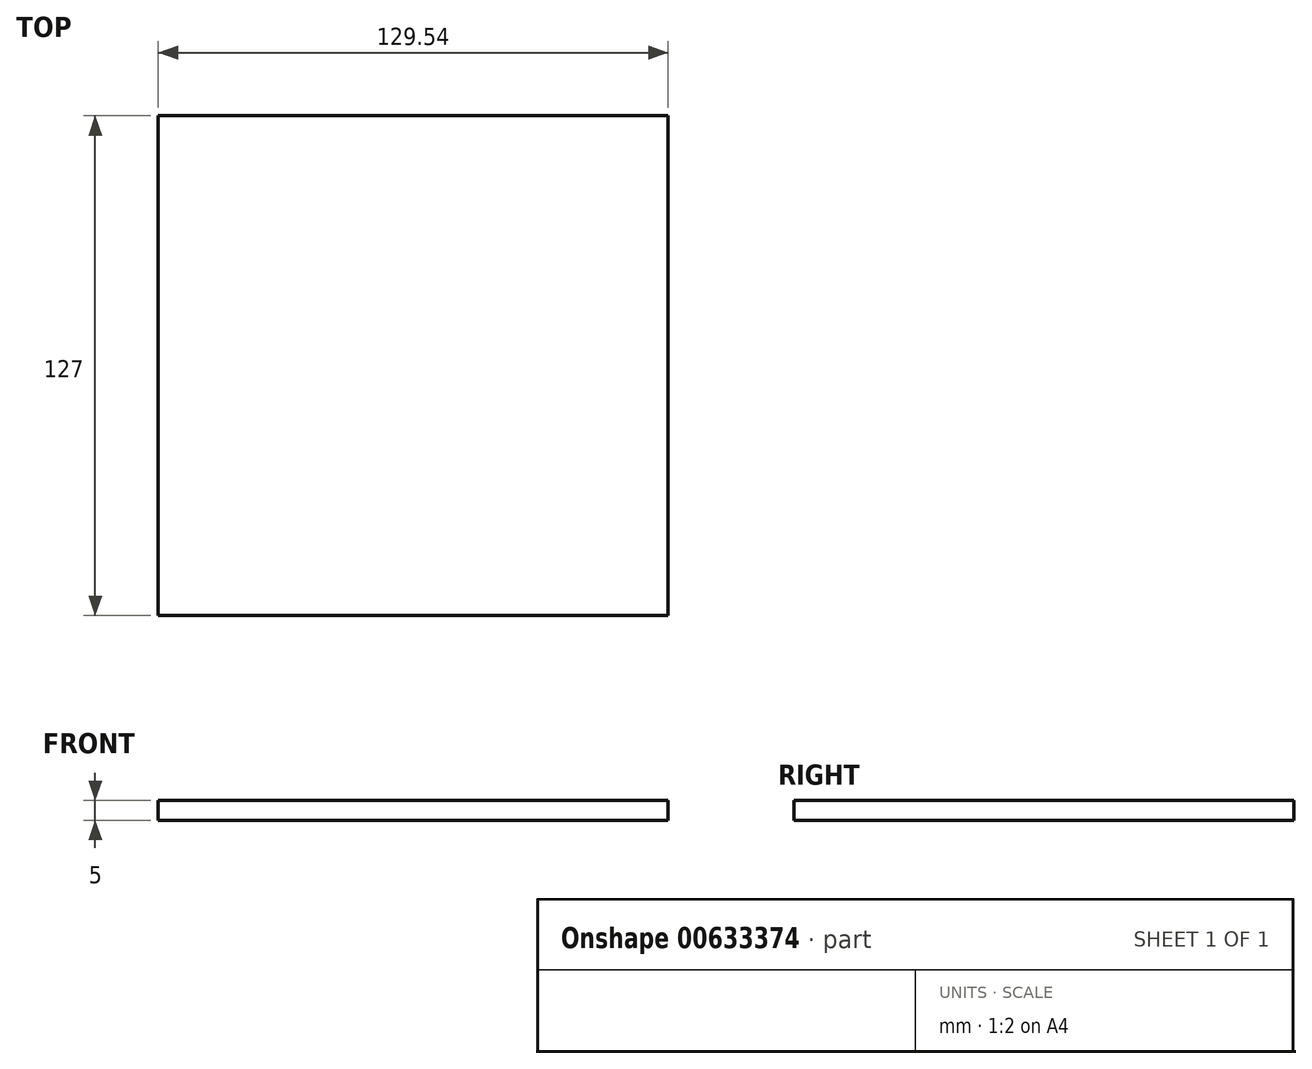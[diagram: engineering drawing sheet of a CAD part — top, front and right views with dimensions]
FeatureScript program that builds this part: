
annotation { "Feature Type Name" : "Feature", "Feature Type Description" : "" }
export const myFeature = defineFeature(function(context is Context, id is Id, definition is map)
    precondition{}
    {
        {
            var Q0;
            Q0=qCreatedBy(makeId("Top.planeOp"),FACE);
            var sketch = newSketch(context, id + "F0", { "sketchPlane" : qUnion([Q0])});
            skLineSegment(sketch, "E0.bottom", {"start": v(64.77, -63.5) * mm, "end": v(-64.77, -63.5) * mm});
            skLineSegment(sketch, "E0.top", {"start": v(64.77, 63.5) * mm, "end": v(-64.77, 63.5) * mm});
            skLineSegment(sketch, "E0.left", {"start": v(64.77, -63.5) * mm, "end": v(64.77, 63.5) * mm});
            skLineSegment(sketch, "E0.right", {"start": v(-64.77, -63.5) * mm, "end": v(-64.77, 63.5) * mm});
            skPoint(sketch, "E0.middle", {"position": v(0, 0) * mm});
            skSolve(sketch);
        }
        {
            var Q0;
            Q0=makeQuery(id+"F0.imprint","IMPRINT",FACE,{"disambiguationData":[TD([[makeQuery(id+"F0.imprint","IMPRINT",EDGE,{"derivedFrom":sQuery(id+"F0.wireOp",EDGE,"E0.bottom")}),-1.0]])]});
            extrude(context, id + "F1", {"entities" : qUnion([Q0]), "depth" : 5 * mm, "offsetDistance" : 25.4 * mm});
        }
    });
